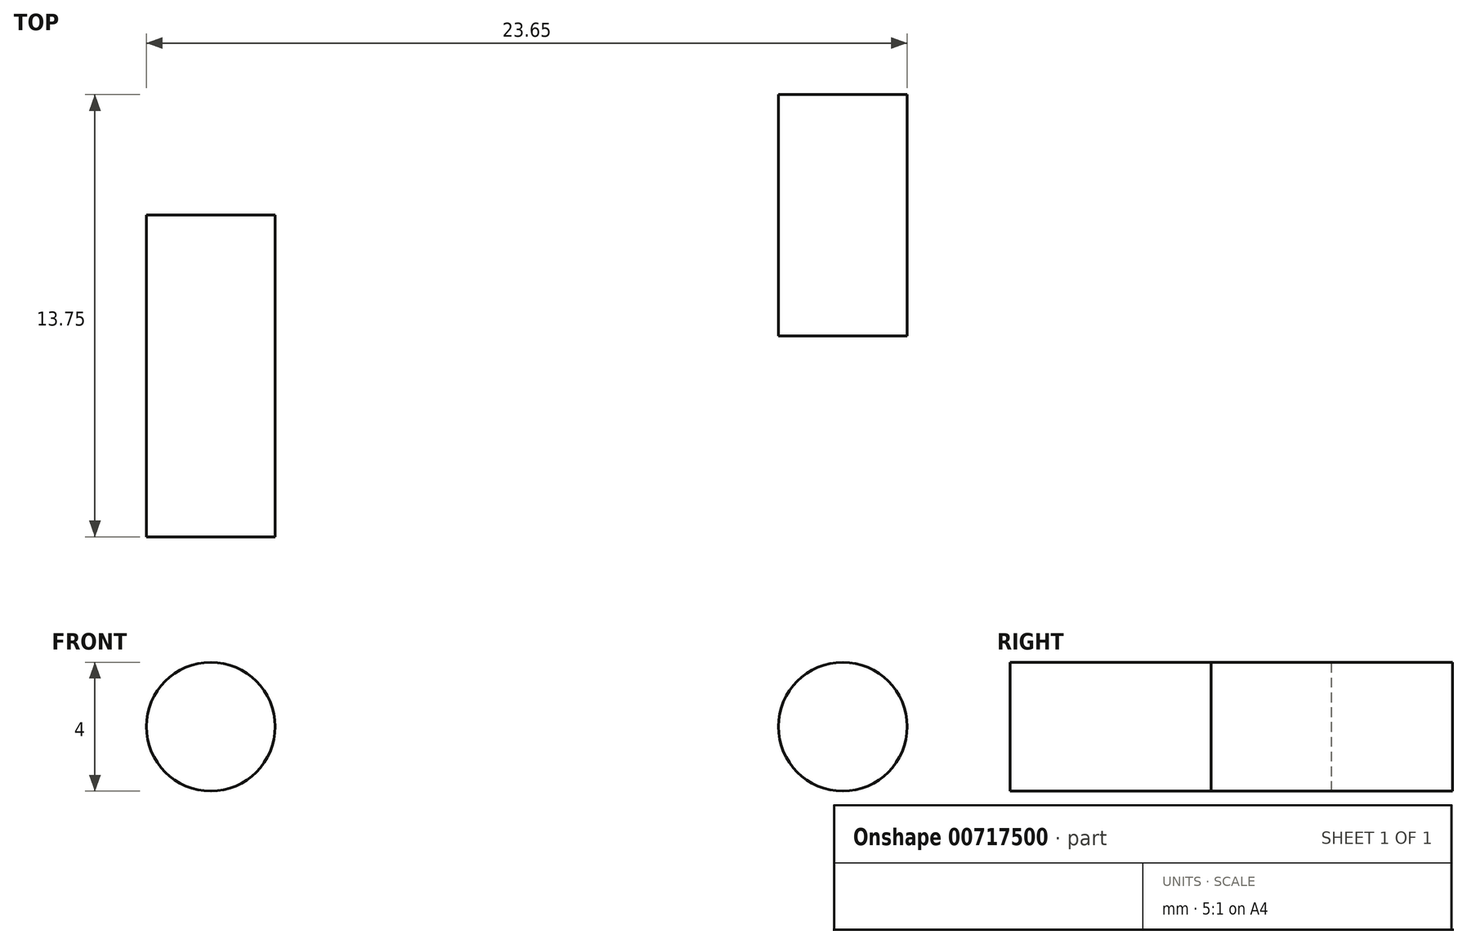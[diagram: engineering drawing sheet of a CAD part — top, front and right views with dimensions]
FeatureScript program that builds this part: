
annotation { "Feature Type Name" : "Feature", "Feature Type Description" : "" }
export const myFeature = defineFeature(function(context is Context, id is Id, definition is map)
    precondition{}
    {
        {
            assignVariable(context, id + "F0", {"name" : "pin1_len", "anyValue" : 7.5});
        }
        {
            assignVariable(context, id + "F1", {"name" : "pin2_len", "anyValue" : 10});
        }
        {
            var Q0;
            Q0=qCreatedBy(makeId("Front.planeOp"),FACE);
            var sketch = newSketch(context, id + "F2", { "sketchPlane" : qUnion([Q0])});
            skCircle(sketch, "E0", {"center": v(0, 0) * mm, "radius": 2 * mm});
            skSolve(sketch);
        }
        {
            var Q0;
            Q0=makeQuery(id+"F2.imprint","IMPRINT",FACE,{"disambiguationData":[TD([[makeQuery(id+"F2.imprint","IMPRINT",EDGE,{"derivedFrom":sQuery(id+"F2.wireOp",EDGE,"E0")}),1.0]])]});
            extrude(context, id + "F3", {"entities" : qUnion([Q0]), "depth" : (getVariable(context, 'pin1_len')) * mm, "offsetDistance" : 25 * mm, "symmetric" : true});
        }
        {
            var Q0;
            Q0=qCreatedBy(makeId("Front.planeOp"),FACE);
            var sketch = newSketch(context, id + "F4", { "sketchPlane" : qUnion([Q0])});
            skCircle(sketch, "E1", {"center": v(-19.65, 0) * mm, "radius": 2 * mm});
            skSolve(sketch);
        }
        {
            var Q0;
            Q0 = qSketchRegion(id + "F4", true);
            extrude(context, id + "F5", {"entities" : qUnion([Q0]), "depth" : (getVariable(context, 'pin2_len')) * mm, "offsetDistance" : 25 * mm});
        }
    });
